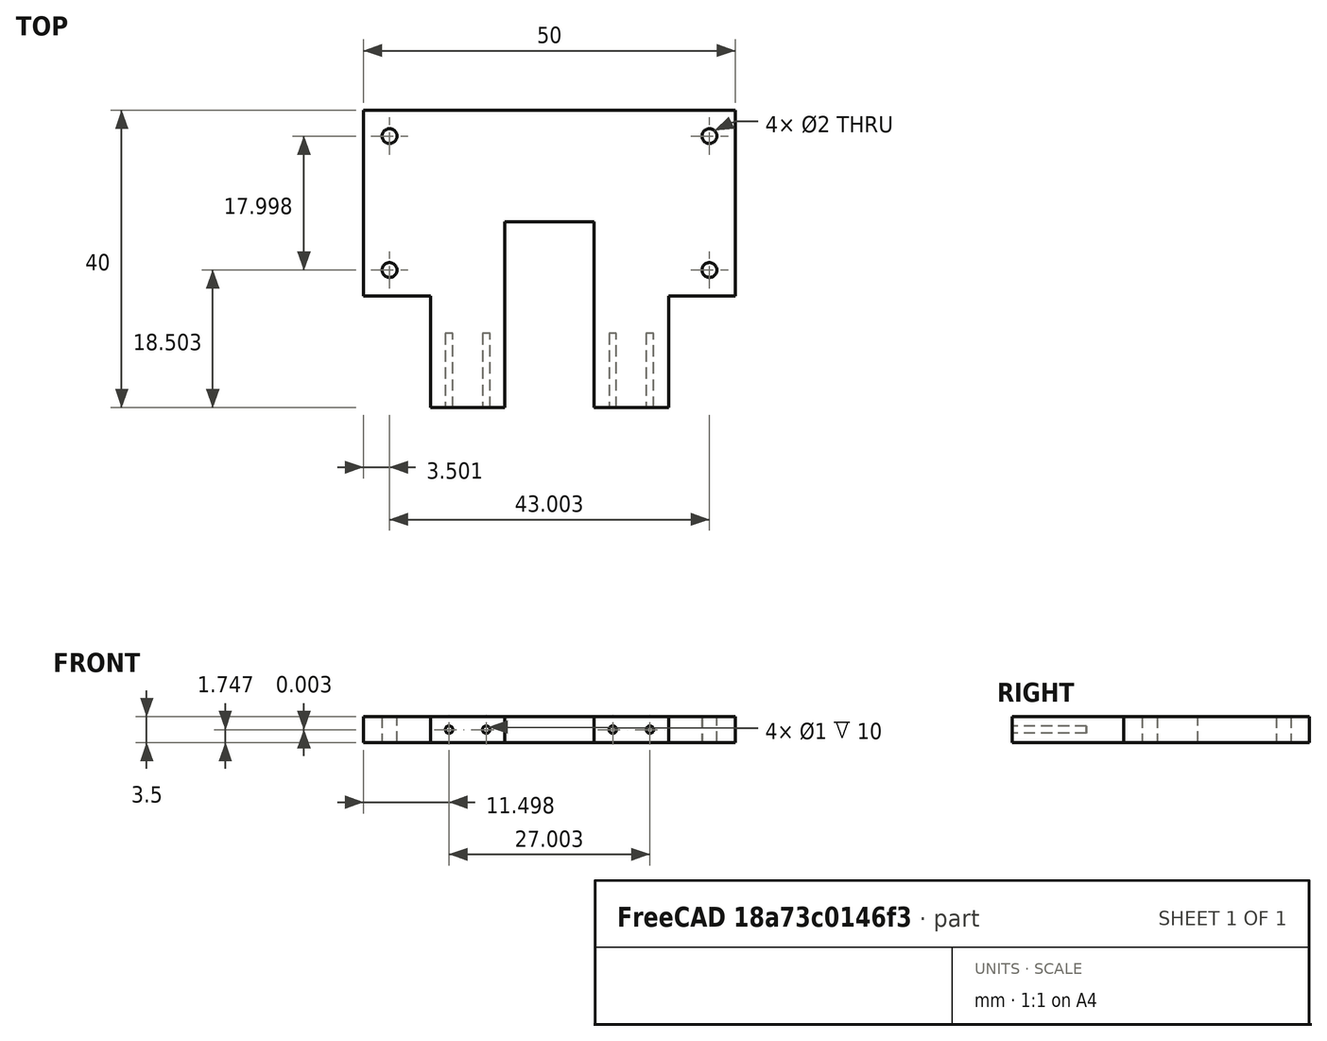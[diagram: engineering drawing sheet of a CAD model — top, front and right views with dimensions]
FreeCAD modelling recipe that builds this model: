
FCSTD DOCUMENT  (FreeCAD 1.0R39109 (Git))
Label: ultrasonic_holder_35mm
License: All rights reserved
LicenseURL: https://en.wikipedia.org/wiki/All_rights_reserved
objects: Sketcher::SketchObject×3, PartDesign::Body×2, PartDesign::Pad×1, PartDesign::Pocket×1
note: 14 computed .brp shape members not serialized (recipe doc carries the construction recipe); baked Part::Feature solids carry a one-line shape summary decoded from their .brp

FEATURE [PartDesign::Body] Body
  AllowCompound = false
  Origin = -> Origin
FEATURE [Sketcher::SketchObject] Sketch
  ArcFitTolerance = 1e-06
  AttachmentSupport = -> [XZ_Plane001]
  FullyConstrained = true
  MakeInternals = false
  MapMode = 5
  Placement = pos=(0,0,0) rot=(1,0,0;1.5708rad)
FEATURE [Sketcher::SketchObject] Sketch001
  ArcFitTolerance = 1e-06
  AttachmentSupport = -> [XY_Plane001]
  FullyConstrained = false
  MakeInternals = false
  MapMode = 5
  sketch-geometry (24):
    g0: LineSegment StartX=9 StartY=0 StartZ=0 EndX=9 EndY=15 EndZ=0
    g1: LineSegment StartX=9 StartY=15 StartZ=0 EndX=0 EndY=15 EndZ=0
    g2: LineSegment StartX=50 StartY=15 StartZ=0 EndX=41 EndY=15 EndZ=0
    g3: LineSegment StartX=41 StartY=15 StartZ=0 EndX=41 EndY=0 EndZ=0
    g4: LineSegment StartX=9 StartY=0 StartZ=0 EndX=19 EndY=0 EndZ=0
    g5: LineSegment StartX=41 StartY=0 StartZ=0 EndX=31 EndY=0 EndZ=0
    g6: LineSegment StartX=0 StartY=40 StartZ=0 EndX=50 EndY=40 EndZ=0
    g7: LineSegment StartX=0 StartY=40 StartZ=0 EndX=0 EndY=15 EndZ=0
    g8: LineSegment StartX=50 StartY=40 StartZ=0 EndX=50 EndY=15 EndZ=0
    g9: LineSegment StartX=31 StartY=25 StartZ=0 EndX=19 EndY=25 EndZ=0
    g10: LineSegment StartX=19 StartY=0 StartZ=0 EndX=19 EndY=25 EndZ=0
    g11: LineSegment StartX=31 StartY=0 StartZ=0 EndX=31 EndY=25 EndZ=0
    g12: GeomPoint X=2.49801 Y=17.5024 Z=0
    g13: GeomPoint X=2.49801 Y=37.4994 Z=0
    g14: GeomPoint X=47.4974 Y=37.4994 Z=0
    g15: GeomPoint X=47.4974 Y=17.5006 Z=0
    g16: GeomPoint X=46.4967 Y=18.5032 Z=0
    g17: GeomPoint X=3.50056 Y=18.5032 Z=0
    g18: GeomPoint X=3.50056 Y=36.5014 Z=0
    g19: GeomPoint X=46.504 Y=36.5014 Z=0
    g20: Circle CenterX=46.504 CenterY=36.5014 CenterZ=0 NormalX=0 NormalY=0 NormalZ=1 AngleXU=0 Radius=1
    g21: Circle CenterX=3.50056 CenterY=36.5014 CenterZ=0 NormalX=0 NormalY=0 NormalZ=1 AngleXU=0 Radius=1
    g22: Circle CenterX=3.50056 CenterY=18.5032 CenterZ=0 NormalX=0 NormalY=0 NormalZ=1 AngleXU=0 Radius=1
    g23: Circle CenterX=46.4967 CenterY=18.5032 CenterZ=0 NormalX=0 NormalY=0 NormalZ=1 AngleXU=0 Radius=1
  constraints (33):
    c: Vertical(g0)
    c: PointOnObject(g0,g-1)
    c: Coincident(g1,g0)
    c: PointOnObject(g1,g-2)
    c: Horizontal(g1)
    c: Horizontal(g2)
    c: Coincident(g3,g2)
    c: PointOnObject(g3,g-1)
    c: Vertical(g3)
    c: Coincident(g4,g0)
    c: PointOnObject(g4,g-1)
    c: Coincident(g5,g3)
    c: PointOnObject(g5,g-1)
    c: Horizontal(g6)
    c: Coincident(g7,g6)
    c: Coincident(g7,g1)
    c: Vertical(g7)
    c: Coincident(g8,g6)
    c: Coincident(g8,g2)
    c: Coincident(g10,g4)
    c: Coincident(g10,g9)
    c: Vertical(g10)
    c: Coincident(g11,g5)
    c: Coincident(g11,g9)
    c: Vertical(g11)
    c: Diameter(g20) = 2
    c: Coincident(g20,g19)
    c: Diameter(g21) = 2
    c: Coincident(g21,g18)
    c: Diameter(g22) = 2
    c: Coincident(g22,g17)
    c: Diameter(g23) = 2
    c: Coincident(g23,g16)
FEATURE [PartDesign::Pad] Pad
  Direction = (0,0,1)
  Length = 3.5
  Length2 = 10
  Profile = -> Sketch001
  ReferenceAxis = -> Sketch001 [N_Axis]
  Refine = true
  Suppressed = false
  Type = 0
FEATURE [Sketcher::SketchObject] Sketch002
  ArcFitTolerance = 1e-06
  AttachmentSupport = -> [Pad]
  FullyConstrained = false
  MakeInternals = false
  MapMode = 5
  Placement = pos=(0,0,0) rot=(1,0,0;1.5708rad)
  sketch-geometry (13):
    g0: GeomPoint X=8.99759 Y=2.49897 Z=0
    g1: GeomPoint X=30.9972 Y=2.50268 Z=0
    g2: GeomPoint X=40.9957 Y=2.49992 Z=0
    g3: GeomPoint X=11.4983 Y=1.75016 Z=0
    g4: GeomPoint X=16.5009 Y=1.75016 Z=0
    g5: GeomPoint X=33.5008 Y=1.74974 Z=0
    g6: GeomPoint X=38.5011 Y=1.74695 Z=0
    g7: Circle CenterX=38.5011 CenterY=1.74695 CenterZ=0 NormalX=0 NormalY=0 NormalZ=1 AngleXU=0 Radius=0.5
    g8: Circle CenterX=33.5008 CenterY=1.74974 CenterZ=0 NormalX=0 NormalY=0 NormalZ=1 AngleXU=0 Radius=0.5
    g9: Circle CenterX=16.5009 CenterY=1.75016 CenterZ=0 NormalX=0 NormalY=0 NormalZ=1 AngleXU=0 Radius=0.5
    g10: Circle CenterX=11.4983 CenterY=1.75016 CenterZ=0 NormalX=0 NormalY=0 NormalZ=1 AngleXU=0 Radius=0.5
    g11: GeomPoint X=8.9998 Y=1.74973 Z=0
    g12: GeomPoint X=40.9999 Y=1.74973 Z=0
  constraints (8):
    c: Diameter(g7) = 1
    c: Coincident(g7,g6)
    c: Diameter(g8) = 1
    c: Coincident(g8,g5)
    c: Diameter(g9) = 1
    c: Coincident(g9,g4)
    c: Diameter(g10) = 1
    c: Coincident(g10,g3)
FEATURE [PartDesign::Pocket] Pocket
  BaseFeature = -> Pad
  Direction = (0,1,-2e-16)
  Length = 10
  Length2 = 5
  Profile = -> Sketch002
  ReferenceAxis = -> Sketch002 [N_Axis]
  Refine = true
  Suppressed = false
  Type = 0
FEATURE [PartDesign::Body] Body001
  AllowCompound = false
  Group = -> [Sketch,Sketch001,Pad,Sketch002,Pocket]
  Origin = -> Origin001
  Tip = -> Pocket
